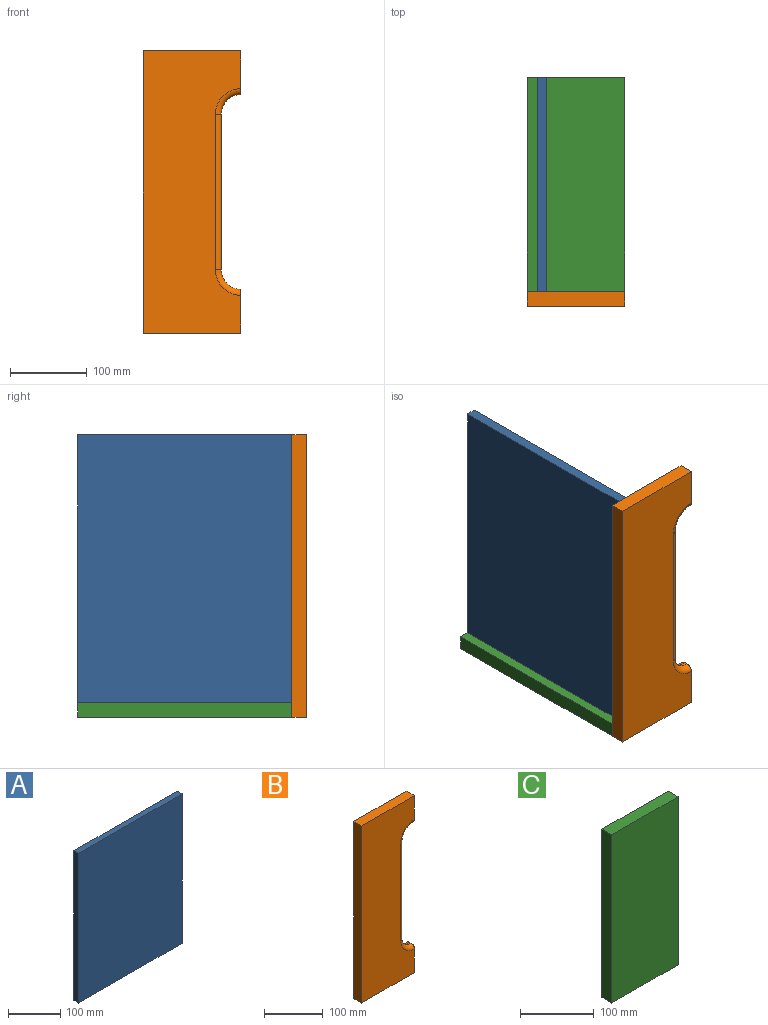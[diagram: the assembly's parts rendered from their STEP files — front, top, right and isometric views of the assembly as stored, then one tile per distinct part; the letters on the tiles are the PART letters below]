
ASSEMBLY  parts=3 mates=2
PART A: 6 faces, bbox 279.4x12.7x349.3 mm
  f0: plane 349.25x12.7mm, normal (-1,0,0), area 4435.5mm2, adj f1,f3,f4,f5
  f1: plane 279.4x12.7mm, normal (0,0,-1), area 3548.4mm2, adj f0,f2,f4,f5
  f2: plane 349.25x12.7mm, normal (1,0,0), area 4435.5mm2, adj f1,f3,f4,f5
  f3: plane 279.4x12.7mm, normal (0,0,1), area 3548.4mm2, adj f0,f2,f4,f5
  f4: plane 349.25x279.4mm, normal (0,-1,0), area 97580.4mm2, adj f0,f1,f2,f3
  f5: plane 349.25x279.4mm, normal (0,1,0), area 97580.4mm2, adj f0,f1,f2,f3
PART B: 16 faces, bbox 127x19.1x368.3 mm
  f0: plane 57.15x19.05mm, normal (1,0,0), area 1063.8mm2, adj f1,f7,f8,f9,f10,f13
  f1: cylinder r=25.4mm len=25.4mm, axis (0,1,0), area 152mm2, adj f0,f2,f10,f13
  f2: plane 203.2x3.81mm, normal (1,0,0), area 774.2mm2, adj f1,f3,f11,f14
  f3: cylinder r=25.4mm len=25.4mm, axis (0,1,0), area 152mm2, adj f2,f4,f12,f15
  f4: plane 57.15x19.05mm, normal (1,0,0), area 1063.8mm2, adj f3,f5,f8,f9,f12,f15
  f5: plane 127x19.05mm, normal (0,0,1), area 2419.3mm2, adj f4,f6,f8,f9
  f6: plane 368.3x19.05mm, normal (-1,0,0), area 7016.1mm2, adj f5,f7,f8,f9
  f7: plane 127x19.05mm, normal (0,0,-1), area 2419.3mm2, adj f0,f6,f8,f9
  f8: plane 368.3x127mm, normal (0,-1,0), area 38351.8mm2, adj f0,f4,f5,f6,f7,f13,f14,f15
  f9: plane 368.3x127mm, normal (0,1,0), area 38351.8mm2, adj f0,f4,f5,f6,f7,f10,f11,f12
  f10: torus R=33.02mm, axis (0,-1,0), area 529.6mm2, adj f0,f1,f9,f11
  f11: cylinder r=7.62mm len=203.2mm, axis (0,0,1), area 2432.2mm2, adj f2,f9,f10,f12
  f12: torus R=33.02mm, axis (0,-1,0), area 529.6mm2, adj f3,f4,f9,f11
  f13: torus R=33.02mm, axis (0,-1,0), area 529.6mm2, adj f0,f1,f8,f14
  f14: cylinder r=7.62mm len=203.2mm, axis (0,0,-1), area 2432.2mm2, adj f2,f8,f13,f15
  f15: torus R=33.02mm, axis (0,-1,0), area 529.6mm2, adj f3,f4,f8,f14
PART C: 6 faces, bbox 127x19.1x279.4 mm
  f0: plane 279.4x19.05mm, normal (-1,0,0), area 5322.6mm2, adj f1,f3,f4,f5
  f1: plane 127x19.05mm, normal (0,0,-1), area 2419.3mm2, adj f0,f2,f4,f5
  f2: plane 279.4x19.05mm, normal (1,0,0), area 5322.6mm2, adj f1,f3,f4,f5
  f3: plane 127x19.05mm, normal (0,0,1), area 2419.3mm2, adj f0,f2,f4,f5
  f4: plane 279.4x127mm, normal (0,-1,0), area 35483.8mm2, adj f0,f1,f2,f3
  f5: plane 279.4x127mm, normal (0,1,0), area 35483.8mm2, adj f0,f1,f2,f3
PLACE A rot(axis=(0,0,-1),90deg) t=(-126.84,191.03,42.44)mm
PLACE B t=(-78.38,70.86,-58.19)mm
PLACE C rot(axis=(1,0,0),90deg) t=(-62.89,251.45,-111.05)mm
MATE fastened C.f3 <-> B.f9  axis (0,-1,0) through (-152.24,70.86,-130.1)mm
MATE fastened A.f2 <-> B.f9  axis (0,-1,0) through (-139.54,70.86,238.2)mm
